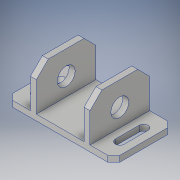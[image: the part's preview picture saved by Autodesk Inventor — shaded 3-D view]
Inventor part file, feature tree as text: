
AUTODESK INVENTOR PART (.ipt)
format: ipt  version: 2019 (Build 230136000, 136)  size: 167,936 bytes
history: native  units: in
note: dims shown in document units (in); Inventor stores cm internally (conversion verified against a paired STEP export)
features: extrude x4, sketch x4, chamfer x2, plane x1, mirror x1
ambient origin geometry x8: Origin, YZ Plane, XZ Plane, XY Plane, X Axis, Y Axis, Z Axis, Center Point
bodies: Solid1 (feature_tree)
feature tree (12):
  extrude  "Extrusion1"  Depth=5.0in
  chamfer  "Chamfer1"  Distance=0.5in
  extrude  "Extrusion2"  Depth=2.0in
  chamfer  "Chamfer2"  Distance=2.0in
  extrude  "Extrusion3"  Depth=0.5in
  extrude  "Extrusion5"  Depth=3.5in TaperAngle=0.0deg
  plane  "Work Plane1"
  mirror  "Mirror1"
  sketch  "Sketch1"  dims[d0=9.0in d1=5.0in d2=0.5in d3=0.0in]
  sketch  "Sketch2"  dims[d4=0.5in d5=0.125in d6=45.0deg d7=2.0in]
  sketch  "Sketch3"  dims[d8=5.0in]
  sketch  "Sketch6"  dims[d9=0.5in d10=2.0in d11=0.5in d12=3.5in d13=0.0in d14=1.0in d15=0.125in d16=45.0deg d17=2.0in d18=1.5in d19=3.0in d20=0.0in d31=0.75in d32=0.75in d33=1.0in d34=0.0in]
